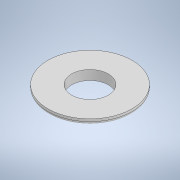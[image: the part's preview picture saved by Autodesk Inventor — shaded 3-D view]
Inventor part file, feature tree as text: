
AUTODESK INVENTOR PART (.ipt)
format: ipt  version: 2021 (Build 250183000, 183)  size: 122,368 bytes
history: native  units: mm
features: extrude x2, sketch x1, fillet x1
ambient origin geometry x8: Origin, YZ Plane, XZ Plane, XY Plane, X Axis, Y Axis, Z Axis, Center Point
bodies: Solid1 (feature_tree)
feature tree (4):
  sketch  "Sketch1"  dims[d2=45.5mm d4=55.0mm d5=4.75mm d6=0.0mm d7=7.0mm d8=0.0mm d9=4.0mm]
  extrude  "Extrusion1"  Depth=4.0mm
  extrude  "Extrusion2"  Depth=4.75mm TaperAngle=0.0deg
  fillet  "Fillet1"  Radius=7.0mm
